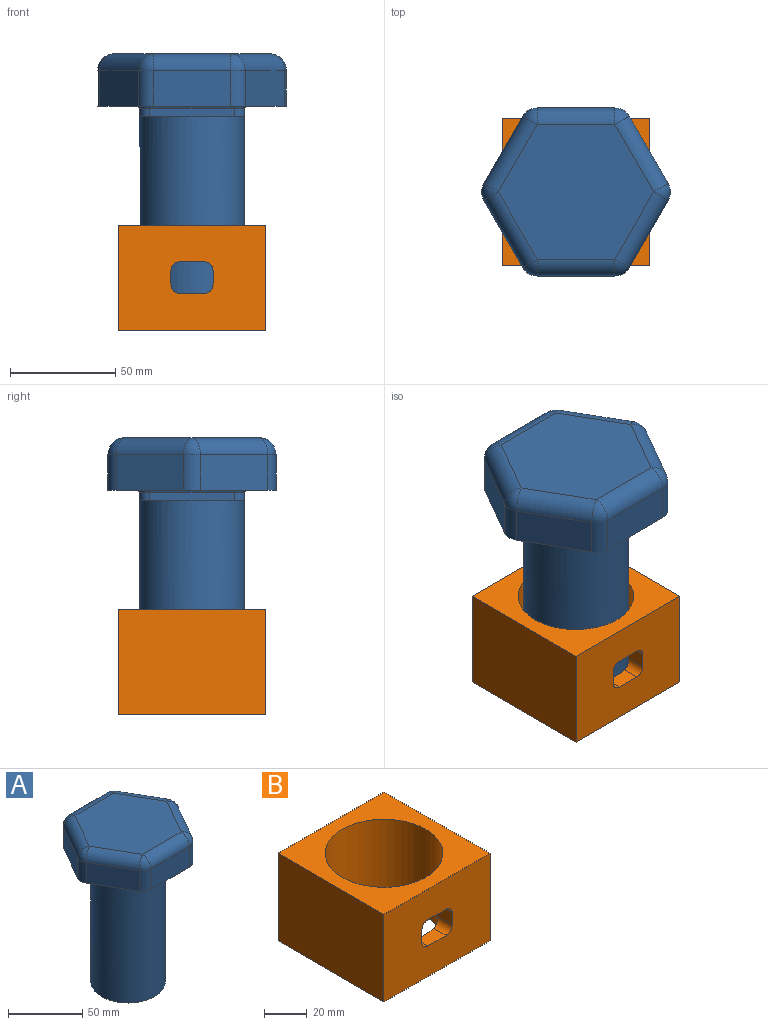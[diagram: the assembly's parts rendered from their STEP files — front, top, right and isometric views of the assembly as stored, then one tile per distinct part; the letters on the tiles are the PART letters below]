
ASSEMBLY  parts=2 mates=1
PART A: 48 faces, bbox 89.9x80x130 mm
  f0: cylinder r=25mm len=100mm, axis (0,0,-1), area 15708mm2, adj f1,f2,f3,f4,f5
  f1: plane 50x50mm, normal (0,0,-1), area 1963.5mm2, adj f0
  f2: plane 25x25mm, normal (0,0,-1), area 128.8mm2, adj f0,f6,f7,f39
  f3: plane 25x25mm, normal (0,0,-1), area 128.8mm2, adj f0,f7,f8,f36
  f4: plane 25x25mm, normal (0,0,-1), area 128.8mm2, adj f0,f8,f9,f37
  f5: plane 25x25mm, normal (0,0,-1), area 128.8mm2, adj f0,f6,f9,f38
  f6: plane 40x4mm, normal (1,0,0), area 160mm2, adj f2,f5,f38,f39,f43
  f7: plane 40x4mm, normal (0,1,0), area 160mm2, adj f2,f3,f36,f39,f40
  f8: plane 40x4mm, normal (-1,0,0), area 160mm2, adj f3,f4,f36,f37,f44
  f9: plane 40x4mm, normal (0,-1,0), area 160mm2, adj f4,f5,f37,f38,f47
  f10: plane 32x18.48mm, normal (-0.87,0.5,0), area 628.2mm2, adj f17,f26,f32,f35
  f11: plane 32x18.48mm, normal (-0.87,-0.5,0), area 628.2mm2, adj f17,f29,f33,f35
  f12: plane 36.95x17mm, normal (0,-1,0), area 628.2mm2, adj f17,f23,f28,f29
  f13: plane 32x18.48mm, normal (0.87,-0.5,0), area 628.2mm2, adj f17,f18,f22,f23
  f14: plane 32x18.48mm, normal (0.87,0.5,0), area 628.2mm2, adj f17,f18,f20,f21
  f15: plane 36.95x17mm, normal (0,1,0), area 628.2mm2, adj f17,f20,f26,f27
  f16: plane 73.9x64mm, normal (0,0,1), area 3547.2mm2, adj f21,f22,f27,f28,f32,f33
  f17: plane 89.9x80mm, normal (0,0,-1), area 2848.8mm2, adj f10,f11,f12,f13,f14,f15,f18,f20
  f18: cylinder r=8mm len=17mm, axis (0,0,-1), area 142.4mm2, adj f13,f14,f17,f19
  f19: sphere r=8mm, area 67mm2, adj f18,f21,f22
  f20: cylinder r=8mm len=17mm, axis (0,0,-1), area 142.4mm2, adj f14,f15,f17,f24
  f21: cylinder r=8mm len=36mm, axis (0.5,-0.87,0), area 464.3mm2, adj f14,f16,f19,f24
  f22: cylinder r=8mm len=36mm, axis (-0.5,-0.87,0), area 464.3mm2, adj f13,f16,f19,f25
  f23: cylinder r=8mm len=17mm, axis (0,0,-1), area 142.4mm2, adj f12,f13,f17,f25
  f24: sphere r=8mm, area 67mm2, adj f20,f21,f27
  f25: sphere r=8mm, area 67mm2, adj f22,f23,f28
  f26: cylinder r=8mm len=17mm, axis (0,0,-1), area 142.4mm2, adj f10,f15,f17,f30
  f27: cylinder r=8mm len=36.95mm, axis (1,0,0), area 464.3mm2, adj f15,f16,f24,f30
  f28: cylinder r=8mm len=36.95mm, axis (-1,0,0), area 464.3mm2, adj f12,f16,f25,f31
  f29: cylinder r=8mm len=17mm, axis (0,0,-1), area 142.4mm2, adj f11,f12,f17,f31
  f30: sphere r=8mm, area 67mm2, adj f26,f27,f32
  f31: sphere r=8mm, area 67mm2, adj f28,f29,f33
  f32: cylinder r=8mm len=36mm, axis (0.5,0.87,0), area 464.3mm2, adj f10,f16,f30,f34
  f33: cylinder r=8mm len=36mm, axis (-0.5,0.87,0), area 464.3mm2, adj f11,f16,f31,f34
  f34: sphere r=8mm, area 67mm2, adj f32,f33,f35
  f35: cylinder r=8mm len=17mm, axis (0,0,-1), area 142.4mm2, adj f10,f11,f17,f34
  f36: cylinder r=5mm len=5mm, axis (0,0,-1), area 31.4mm2, adj f3,f7,f8,f42
  f37: cylinder r=5mm len=5mm, axis (0,0,1), area 31.4mm2, adj f4,f8,f9,f46
  f38: cylinder r=5mm len=5mm, axis (0,0,-1), area 31.4mm2, adj f5,f6,f9,f45
  f39: cylinder r=5mm len=5mm, axis (0,0,1), area 31.4mm2, adj f2,f6,f7,f41
  f40: cylinder r=1mm len=40mm, axis (1,0,0), area 62.8mm2, adj f7,f17,f41,f42
  f41: torus R=6mm, axis (0,0,1), area 13.2mm2, adj f17,f39,f40,f43
  f42: torus R=6mm, axis (0,0,1), area 13.2mm2, adj f17,f36,f40,f44
  f43: cylinder r=1mm len=40mm, axis (0,-1,0), area 62.8mm2, adj f6,f17,f41,f45
  f44: cylinder r=1mm len=40mm, axis (0,1,0), area 62.8mm2, adj f8,f17,f42,f46
  f45: torus R=6mm, axis (0,0,1), area 13.2mm2, adj f17,f38,f43,f47
  f46: torus R=6mm, axis (0,0,1), area 13.2mm2, adj f17,f37,f44,f47
  f47: cylinder r=1mm len=40mm, axis (-1,0,0), area 62.8mm2, adj f9,f17,f45,f46
PART B: 15 faces, bbox 70x70x50 mm
  f0: plane 70x50mm, normal (1,0,0), area 3500mm2, adj f1,f4,f5,f6
  f1: plane 70x50mm, normal (0,1,0), area 3500mm2, adj f0,f2,f5,f6
  f2: plane 70x50mm, normal (-1,0,0), area 3500mm2, adj f1,f4,f5,f6
  f3: cylinder r=27.5mm len=55mm, axis (0,0,-1), area 8346.9mm2, adj f5,f6,f7,f8,f9,f10,f11,f12
  f4: plane 70x50mm, normal (0,-1,0), area 3213.7mm2, adj f0,f2,f5,f6,f7,f8,f9,f10
  f5: plane 70x70mm, normal (0,0,1), area 2524.2mm2, adj f0,f1,f2,f3,f4
  f6: plane 70x70mm, normal (0,0,-1), area 2524.2mm2, adj f0,f1,f2,f3,f4
  f7: plane 9.38x7mm, normal (1,0,0), area 65.7mm2, adj f3,f4,f11,f14
  f8: plane 12x8.16mm, normal (0,0,1), area 92.6mm2, adj f3,f4,f11,f12
  f9: plane 9.38x7mm, normal (-1,0,0), area 65.7mm2, adj f3,f4,f12,f13
  f10: plane 12x8.16mm, normal (0,0,-1), area 92.6mm2, adj f3,f4,f13,f14
  f11: cylinder r=4mm len=9.38mm, axis (0,1,0), area 55.9mm2, adj f3,f4,f7,f8
  f12: cylinder r=4mm len=9.38mm, axis (0,-1,0), area 55.9mm2, adj f3,f4,f8,f9
  f13: cylinder r=4mm len=9.38mm, axis (0,1,0), area 55.9mm2, adj f3,f4,f9,f10
  f14: cylinder r=4mm len=9.38mm, axis (0,-1,0), area 55.9mm2, adj f3,f4,f7,f10
PLACE A t=(-107.19,-81.2,-12.92)mm
PLACE B t=(-107.19,-81.2,-14.49)mm fixed
MATE slider A.f0 <-> B.f3  axis (0,0,-1) through (-107.19,-81.2,-12.92)mm
